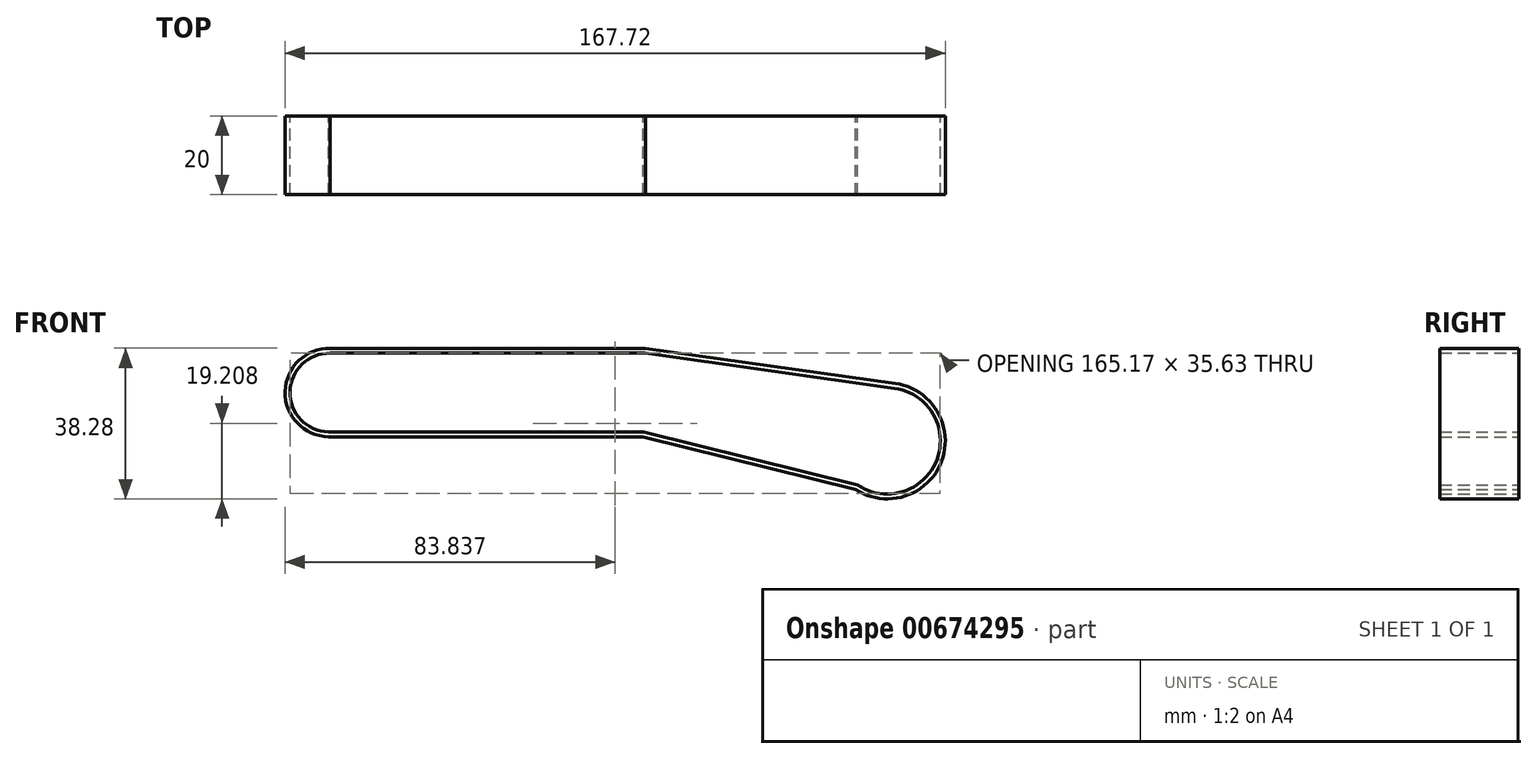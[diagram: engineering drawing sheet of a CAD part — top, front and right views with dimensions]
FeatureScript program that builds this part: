
annotation { "Feature Type Name" : "Feature", "Feature Type Description" : "" }
export const myFeature = defineFeature(function(context is Context, id is Id, definition is map)
    precondition{}
    {
        {
            var Q0;
            Q0=qCreatedBy(makeId("Front.planeOp"),FACE);
            var sketch = newSketch(context, id + "F0", { "sketchPlane" : qUnion([Q0])});
            skLineSegment(sketch, "E0", {"start": v(-46.26, 8.78) * mm, "end": v(33.74, 8.78) * mm});
            skLineSegment(sketch, "E1", {"start": v(-46.7, -11.21) * mm, "end": v(33.3, -11.21) * mm});
            skArc(sketch, "E2", {"start": v(-46.26, 8.78) * mm, "mid": v(-56.48, -1) * mm, "end": v(-46.7, -11.21) * mm});
            skLineSegment(sketch, "E3", {"start": v(33.74, 8.78) * mm, "end": v(97.12, -0.12) * mm});
            skLineSegment(sketch, "E4", {"start": v(33.3, -11.21) * mm, "end": v(87.66, -24.66) * mm});
            skArc(sketch, "E5", {"start": v(87.66, -24.66) * mm, "mid": v(107.83, -18.35) * mm, "end": v(97.12, -0.12) * mm});
            skLineSegment(sketch, "E6.0", {"start": v(34, 10) * mm, "end": v(97.3, 1.11) * mm});
            skLineSegment(sketch, "E7.0", {"start": v(33.14, -12.46) * mm, "end": v(87.14, -25.82) * mm});
            skArc(sketch, "E8.0", {"start": v(87.14, -25.82) * mm, "mid": v(109.04, -18.7) * mm, "end": v(97.3, 1.11) * mm});
            skLineSegment(sketch, "E9.0", {"start": v(-46.25, 10.03) * mm, "end": v(33.74, 10.03) * mm});
            skArc(sketch, "E9.1", {"start": v(-46.25, 10.03) * mm, "mid": v(-57.73, -0.98) * mm, "end": v(-46.72, -12.46) * mm});
            skLineSegment(sketch, "E9.2", {"start": v(-46.72, -12.46) * mm, "end": v(33.14, -12.46) * mm});
            skLineSegment(sketch, "E10", {"start": v(33.74, 10.03) * mm, "end": v(33.83, 10.03) * mm});
            skLineSegment(sketch, "E11", {"start": v(34, 10) * mm, "end": v(33.83, 10.03) * mm});
            skSolve(sketch);
        }
        {
            var Q0;
            Q0 = qSketchRegion(id + "F0", true);
            extrude(context, id + "F1", {"entities" : qUnion([Q0]), "depth" : 20 * mm, "offsetDistance" : 25 * mm});
        }
    });
